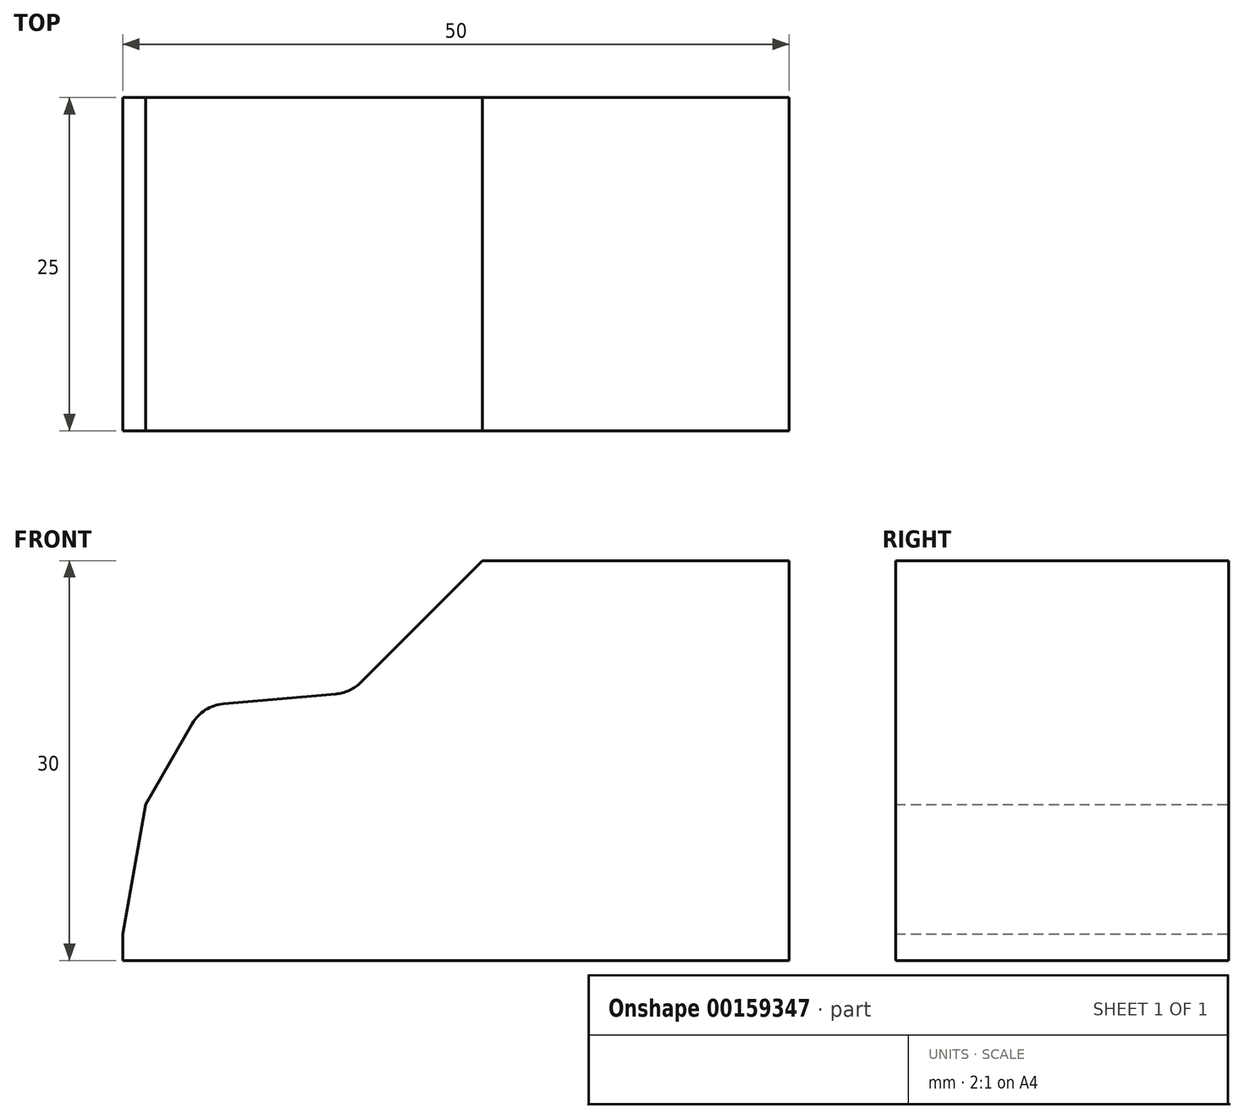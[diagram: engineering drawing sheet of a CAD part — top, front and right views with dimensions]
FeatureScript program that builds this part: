
annotation { "Feature Type Name" : "Feature", "Feature Type Description" : "" }
export const myFeature = defineFeature(function(context is Context, id is Id, definition is map)
    precondition{}
    {
        {
            var Q0;
            Q0=qCreatedBy(makeId("Front.planeOp"),FACE);
            var sketch = newSketch(context, id + "F0", { "sketchPlane" : qUnion([Q0])});
            skLineSegment(sketch, "E0", {"start": v(0, 0) * mm, "end": v(50, 0) * mm});
            skLineSegment(sketch, "E1", {"start": v(50, 0) * mm, "end": v(50, 30) * mm});
            skLineSegment(sketch, "E2", {"start": v(50, 30) * mm, "end": v(27, 30) * mm});
            skLineSegment(sketch, "E3", {"start": v(27, 30) * mm, "end": v(17.87, 20.87) * mm});
            skLineSegment(sketch, "E4", {"start": v(0, 0) * mm, "end": v(0, 2) * mm});
            skLineSegment(sketch, "E5", {"start": v(0, 2) * mm, "end": v(1.71, 11.7) * mm});
            skLineSegment(sketch, "E6", {"start": v(0, 2) * mm, "end": v(0, 29.3) * mm, "construction": true});
            skLineSegment(sketch, "E7", {"start": v(1.71, 11.7) * mm, "end": v(5.21, 17.77) * mm});
            skLineSegment(sketch, "E8", {"start": v(7.55, 19.26) * mm, "end": v(16, 20) * mm});
            skPoint(sketch, "E9.visualSharp", {"position": v(6, 19.12) * mm});
            skArc(sketch, "E9.filletArc", {"start": v(7.55, 19.26) * mm, "mid": v(6.2, 18.8) * mm, "end": v(5.21, 17.77) * mm});
            skPoint(sketch, "E10.newPointA", {"position": v(17, 20) * mm});
            skArc(sketch, "E10.filletArc", {"start": v(16, 20) * mm, "mid": v(17.01, 20.27) * mm, "end": v(17.87, 20.87) * mm});
            skLineSegment(sketch, "E11", {"start": v(1.71, 11.7) * mm, "end": v(8.6, 23.64) * mm, "construction": true});
            skPoint(sketch, "E12", {"position": v(6.5, 20) * mm});
            skLineSegment(sketch, "E13", {"start": v(17, 20) * mm, "end": v(-8.02, 20) * mm, "construction": true});
            skSolve(sketch);
        }
        {
            var Q0;
            Q0=makeQuery(id+"F0.imprint","IMPRINT",FACE,{"disambiguationData":[TD([[makeQuery(id+"F0.imprint","IMPRINT",EDGE,{"derivedFrom":sQuery(id+"F0.wireOp",EDGE,"E0")}),1.0]])]});
            extrude(context, id + "F1", {"entities" : qUnion([Q0]), "depth" : 25 * mm, "offsetDistance" : 25 * mm});
        }
    });
